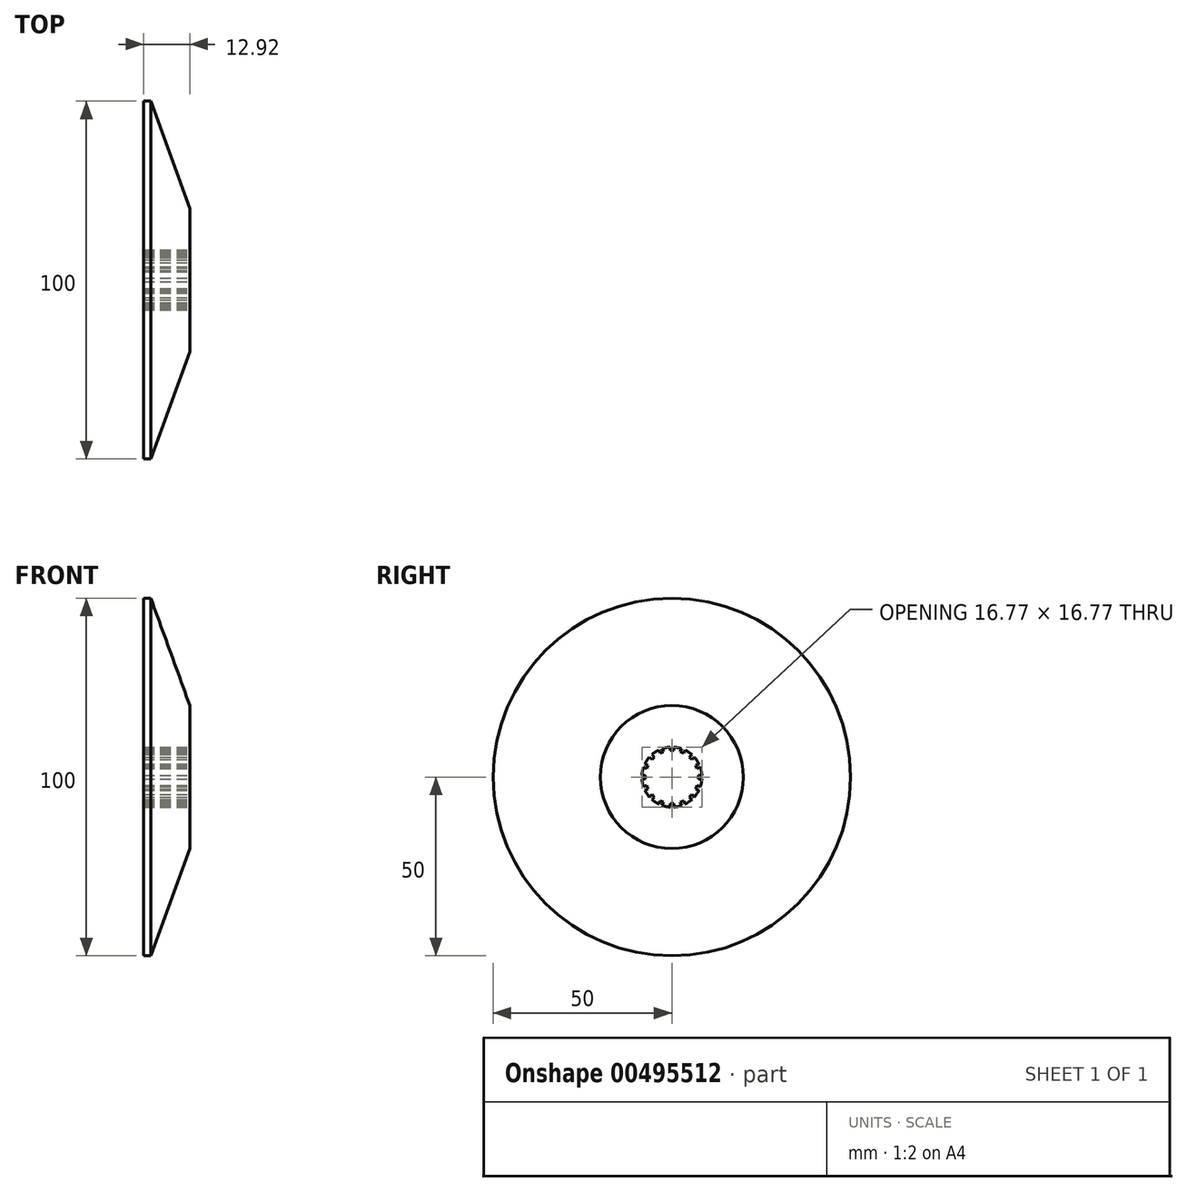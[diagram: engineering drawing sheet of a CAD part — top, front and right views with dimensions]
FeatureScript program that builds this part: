
annotation { "Feature Type Name" : "Feature", "Feature Type Description" : "" }
export const myFeature = defineFeature(function(context is Context, id is Id, definition is map)
    precondition{}
    {
        {
            var Q0;
            Q0=qCreatedBy(makeId("Front.planeOp"),FACE);
            var sketch = newSketch(context, id + "F0", { "sketchPlane" : qUnion([Q0])});
            skLineSegment(sketch, "E0", {"start": v(0, 0) * mm, "end": v(0, 20) * mm});
            skLineSegment(sketch, "E1", {"start": v(0, 20) * mm, "end": v(-10.92, 50) * mm});
            skLineSegment(sketch, "E2", {"start": v(-10.92, 50) * mm, "end": v(-12.92, 50) * mm});
            skLineSegment(sketch, "E3", {"start": v(-12.92, 50) * mm, "end": v(-12.92, 0) * mm});
            skLineSegment(sketch, "E4", {"start": v(-12.92, 0) * mm, "end": v(0, 0) * mm});
            skSolve(sketch);
        }
        {
            var Q0;
            Q0=qSketchRegion(id+"F0",true);
            var Q1;
            Q1=sQuery(id+"F0.wireOp",EDGE,"E4");
            revolve(context, id + "F1", {"entities" : qUnion([Q0]), "axis" : qUnion([Q1]), "revolveType" : RevolveType.FULL});
        }
        {
            var Q0;
            Q0=qCreatedBy(makeId("Right.planeOp"),FACE);
            var sketch = newSketch(context, id + "F2", { "sketchPlane" : qUnion([Q0])});
            skPoint(sketch, "E5", {"position": v(0, 0) * mm});
            skSolve(sketch);
        }
        {
            var Q0;
            Q0=sQuery(id+"F2.wireOp",VERTEX,"E5");
            var Q1;
            Q1=makeQuery(id+"F1.opRevolve","SWEPT_BODY",BODY,{"disambiguationData":[OSD([sQuery(id+"F0.wireOp",EDGE,"E0"),sQuery(id+"F0.wireOp",EDGE,"E1"),sQuery(id+"F0.wireOp",EDGE,"E2"),sQuery(id+"F0.wireOp",EDGE,"E3"),sQuery(id+"F0.wireOp",EDGE,"E4")])]});
            hole(context, id + "F3", {"style" : HoleStyle.SIMPLE, "endStyle" : HoleEndStyle.THROUGH, "holeDiameter" : 16.8 * mm, "isTappedThrough" : true, "tappedDepth" : 12 * mm, "tapClearance" : 3, "locations" : qUnion([Q0]), "scope" : qUnion([Q1])});
        }
        {
            var Q0;
            Q0=qCreatedBy(makeId("Right.planeOp"),FACE);
            var sketch = newSketch(context, id + "F4", { "sketchPlane" : qUnion([Q0])});
            skArc(sketch, "E6", {"start": v(0.5, 8.39) * mm, "mid": v(0, 8.4) * mm, "end": v(-0.5, 8.39) * mm});
            skLineSegment(sketch, "E7.top", {"start": v(0.5, 7.4) * mm, "end": v(-0.5, 7.4) * mm});
            skLineSegment(sketch, "E7.left", {"start": v(0.5, 8.39) * mm, "end": v(0.5, 7.4) * mm});
            skLineSegment(sketch, "E7.right", {"start": v(-0.5, 8.39) * mm, "end": v(-0.5, 7.4) * mm});
            skPoint(sketch, "E7.middle", {"position": v(0, 8.4) * mm});
            skPoint(sketch, "E8.1.0", {"position": v(-3.21, 7.76) * mm});
            skArc(sketch, "E8.1.1", {"start": v(-2.75, 7.94) * mm, "mid": v(-3.21, 7.76) * mm, "end": v(-3.67, 7.56) * mm});
            skLineSegment(sketch, "E8.1.2", {"start": v(-2.37, 7.03) * mm, "end": v(-3.3, 6.65) * mm});
            skLineSegment(sketch, "E8.1.3", {"start": v(-2.75, 7.94) * mm, "end": v(-2.37, 7.03) * mm});
            skLineSegment(sketch, "E8.1.4", {"start": v(-3.67, 7.56) * mm, "end": v(-3.3, 6.65) * mm});
            skPoint(sketch, "E8.2.0", {"position": v(-5.94, 5.94) * mm});
            skArc(sketch, "E8.2.1", {"start": v(-5.58, 6.28) * mm, "mid": v(-5.94, 5.94) * mm, "end": v(-6.28, 5.58) * mm});
            skLineSegment(sketch, "E8.2.2", {"start": v(-4.88, 5.59) * mm, "end": v(-5.59, 4.88) * mm});
            skLineSegment(sketch, "E8.2.3", {"start": v(-5.58, 6.28) * mm, "end": v(-4.88, 5.59) * mm});
            skLineSegment(sketch, "E8.2.4", {"start": v(-6.28, 5.58) * mm, "end": v(-5.59, 4.88) * mm});
            skArc(sketch, "E9.1.3.0", {"start": v(-7.56, 3.67) * mm, "mid": v(-7.76, 3.21) * mm, "end": v(-7.94, 2.75) * mm});
            skLineSegment(sketch, "E9.5.3.0", {"start": v(-6.65, 3.3) * mm, "end": v(-7.03, 2.37) * mm});
            skPoint(sketch, "E9.7.3.0", {"position": v(-7.76, 3.21) * mm});
            skLineSegment(sketch, "E9.8.3.0", {"start": v(-7.56, 3.67) * mm, "end": v(-6.65, 3.3) * mm});
            skLineSegment(sketch, "E9.11.3.0", {"start": v(-7.94, 2.75) * mm, "end": v(-7.03, 2.37) * mm});
            skArc(sketch, "E9.1.4.0", {"start": v(-8.39, 0.5) * mm, "mid": v(-8.4, 0) * mm, "end": v(-8.39, -0.5) * mm});
            skLineSegment(sketch, "E9.5.4.0", {"start": v(-7.4, 0.5) * mm, "end": v(-7.4, -0.5) * mm});
            skPoint(sketch, "E9.7.4.0", {"position": v(-8.4, 0) * mm});
            skLineSegment(sketch, "E9.8.4.0", {"start": v(-8.39, 0.5) * mm, "end": v(-7.4, 0.5) * mm});
            skLineSegment(sketch, "E9.11.4.0", {"start": v(-8.39, -0.5) * mm, "end": v(-7.4, -0.5) * mm});
            skArc(sketch, "E9.1.5.0", {"start": v(-7.94, -2.75) * mm, "mid": v(-7.76, -3.21) * mm, "end": v(-7.56, -3.67) * mm});
            skLineSegment(sketch, "E9.5.5.0", {"start": v(-7.03, -2.37) * mm, "end": v(-6.65, -3.3) * mm});
            skPoint(sketch, "E9.7.5.0", {"position": v(-7.76, -3.21) * mm});
            skLineSegment(sketch, "E9.8.5.0", {"start": v(-7.94, -2.75) * mm, "end": v(-7.03, -2.37) * mm});
            skLineSegment(sketch, "E9.11.5.0", {"start": v(-7.56, -3.67) * mm, "end": v(-6.65, -3.3) * mm});
            skArc(sketch, "E9.1.6.0", {"start": v(-6.28, -5.58) * mm, "mid": v(-5.94, -5.94) * mm, "end": v(-5.58, -6.28) * mm});
            skLineSegment(sketch, "E9.5.6.0", {"start": v(-5.59, -4.88) * mm, "end": v(-4.88, -5.59) * mm});
            skPoint(sketch, "E9.7.6.0", {"position": v(-5.94, -5.94) * mm});
            skLineSegment(sketch, "E9.8.6.0", {"start": v(-6.28, -5.58) * mm, "end": v(-5.59, -4.88) * mm});
            skLineSegment(sketch, "E9.11.6.0", {"start": v(-5.58, -6.28) * mm, "end": v(-4.88, -5.59) * mm});
            skArc(sketch, "E9.1.7.0", {"start": v(-3.67, -7.56) * mm, "mid": v(-3.21, -7.76) * mm, "end": v(-2.75, -7.94) * mm});
            skLineSegment(sketch, "E9.5.7.0", {"start": v(-3.3, -6.65) * mm, "end": v(-2.37, -7.03) * mm});
            skPoint(sketch, "E9.7.7.0", {"position": v(-3.21, -7.76) * mm});
            skLineSegment(sketch, "E9.8.7.0", {"start": v(-3.67, -7.56) * mm, "end": v(-3.3, -6.65) * mm});
            skLineSegment(sketch, "E9.11.7.0", {"start": v(-2.75, -7.94) * mm, "end": v(-2.37, -7.03) * mm});
            skArc(sketch, "E10.1.8.0", {"start": v(-0.5, -8.39) * mm, "mid": v(0, -8.4) * mm, "end": v(0.5, -8.39) * mm});
            skLineSegment(sketch, "E10.5.8.0", {"start": v(-0.5, -7.4) * mm, "end": v(0.5, -7.4) * mm});
            skPoint(sketch, "E10.7.8.0", {"position": v(0, -8.4) * mm});
            skLineSegment(sketch, "E10.8.8.0", {"start": v(-0.5, -8.39) * mm, "end": v(-0.5, -7.4) * mm});
            skLineSegment(sketch, "E10.11.8.0", {"start": v(0.5, -8.39) * mm, "end": v(0.5, -7.4) * mm});
            skArc(sketch, "E10.1.9.0", {"start": v(2.75, -7.94) * mm, "mid": v(3.21, -7.76) * mm, "end": v(3.67, -7.56) * mm});
            skLineSegment(sketch, "E10.5.9.0", {"start": v(2.37, -7.03) * mm, "end": v(3.3, -6.65) * mm});
            skPoint(sketch, "E10.7.9.0", {"position": v(3.21, -7.76) * mm});
            skLineSegment(sketch, "E10.8.9.0", {"start": v(2.75, -7.94) * mm, "end": v(2.37, -7.03) * mm});
            skLineSegment(sketch, "E10.11.9.0", {"start": v(3.67, -7.56) * mm, "end": v(3.3, -6.65) * mm});
            skArc(sketch, "E10.1.10.0", {"start": v(5.58, -6.28) * mm, "mid": v(5.94, -5.94) * mm, "end": v(6.28, -5.58) * mm});
            skLineSegment(sketch, "E10.5.10.0", {"start": v(4.88, -5.59) * mm, "end": v(5.59, -4.88) * mm});
            skPoint(sketch, "E10.7.10.0", {"position": v(5.94, -5.94) * mm});
            skLineSegment(sketch, "E10.8.10.0", {"start": v(5.58, -6.28) * mm, "end": v(4.88, -5.59) * mm});
            skLineSegment(sketch, "E10.11.10.0", {"start": v(6.28, -5.58) * mm, "end": v(5.59, -4.88) * mm});
            skArc(sketch, "E10.1.11.0", {"start": v(7.56, -3.67) * mm, "mid": v(7.76, -3.21) * mm, "end": v(7.94, -2.75) * mm});
            skLineSegment(sketch, "E10.5.11.0", {"start": v(6.65, -3.3) * mm, "end": v(7.03, -2.37) * mm});
            skPoint(sketch, "E10.7.11.0", {"position": v(7.76, -3.21) * mm});
            skLineSegment(sketch, "E10.8.11.0", {"start": v(7.56, -3.67) * mm, "end": v(6.65, -3.3) * mm});
            skLineSegment(sketch, "E10.11.11.0", {"start": v(7.94, -2.75) * mm, "end": v(7.03, -2.37) * mm});
            skArc(sketch, "E10.1.12.0", {"start": v(8.39, -0.5) * mm, "mid": v(8.4, 0) * mm, "end": v(8.39, 0.5) * mm});
            skLineSegment(sketch, "E10.5.12.0", {"start": v(7.4, -0.5) * mm, "end": v(7.4, 0.5) * mm});
            skPoint(sketch, "E10.7.12.0", {"position": v(8.4, 0) * mm});
            skLineSegment(sketch, "E10.8.12.0", {"start": v(8.39, -0.5) * mm, "end": v(7.4, -0.5) * mm});
            skLineSegment(sketch, "E10.11.12.0", {"start": v(8.39, 0.5) * mm, "end": v(7.4, 0.5) * mm});
            skArc(sketch, "E10.1.13.0", {"start": v(7.94, 2.75) * mm, "mid": v(7.76, 3.21) * mm, "end": v(7.56, 3.67) * mm});
            skLineSegment(sketch, "E10.5.13.0", {"start": v(7.03, 2.37) * mm, "end": v(6.65, 3.3) * mm});
            skPoint(sketch, "E10.7.13.0", {"position": v(7.76, 3.21) * mm});
            skLineSegment(sketch, "E10.8.13.0", {"start": v(7.94, 2.75) * mm, "end": v(7.03, 2.37) * mm});
            skLineSegment(sketch, "E10.11.13.0", {"start": v(7.56, 3.67) * mm, "end": v(6.65, 3.3) * mm});
            skArc(sketch, "E10.1.14.0", {"start": v(6.28, 5.58) * mm, "mid": v(5.94, 5.94) * mm, "end": v(5.58, 6.28) * mm});
            skLineSegment(sketch, "E10.5.14.0", {"start": v(5.59, 4.88) * mm, "end": v(4.88, 5.59) * mm});
            skPoint(sketch, "E10.7.14.0", {"position": v(5.94, 5.94) * mm});
            skLineSegment(sketch, "E10.8.14.0", {"start": v(6.28, 5.58) * mm, "end": v(5.59, 4.88) * mm});
            skLineSegment(sketch, "E10.11.14.0", {"start": v(5.58, 6.28) * mm, "end": v(4.88, 5.59) * mm});
            skArc(sketch, "E10.1.15.0", {"start": v(3.67, 7.56) * mm, "mid": v(3.21, 7.76) * mm, "end": v(2.75, 7.94) * mm});
            skLineSegment(sketch, "E10.5.15.0", {"start": v(3.3, 6.65) * mm, "end": v(2.37, 7.03) * mm});
            skPoint(sketch, "E10.7.15.0", {"position": v(3.21, 7.76) * mm});
            skLineSegment(sketch, "E10.8.15.0", {"start": v(3.67, 7.56) * mm, "end": v(3.3, 6.65) * mm});
            skLineSegment(sketch, "E10.11.15.0", {"start": v(2.75, 7.94) * mm, "end": v(2.37, 7.03) * mm});
            skSolve(sketch);
        }
        {
            var Q0;
            Q0=qSketchRegion(id+"F4",true);
            extrude(context, id + "F5", {"entities" : qUnion([Q0]), "operationType" : NewBodyOperationType.ADD, "oppositeDirection" : true, "depth" : 12.92 * mm});
        }
    });
